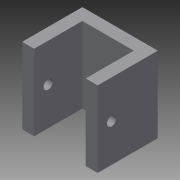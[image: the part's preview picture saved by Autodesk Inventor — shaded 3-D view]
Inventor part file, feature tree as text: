
AUTODESK INVENTOR PART (.ipt)
format: ipt  version: 2013 (Build 170138000, 138)  size: 106,496 bytes
history: native  units: in
note: dims shown in document units (in); Inventor stores cm internally (conversion verified against a paired STEP export)
features: extrude x4, sketch x4
ambient origin geometry x8: Origin, YZ Plane, XZ Plane, XY Plane, X Axis, Y Axis, Z Axis, Center Point
bodies: Solid1 (feature_tree)
feature tree (8):
  extrude  "Extrusion1"  Depth=1.5748in
  extrude  "Extrusion2"  Depth=0.25in
  extrude  "Extrusion3"  Depth=0.25in
  extrude  "Extrusion4"  Depth=0.19in
  sketch  "Sketch1"  dims[d0=1.68in d1=1.5748in]
  sketch  "Sketch2"  dims[d2=0.25in d3=0.0in d4=0.25in]
  sketch  "Sketch3"  dims[d5=1.0in d6=0.0in d7=0.25in]
  sketch  "Sketch4"  dims[d8=1.0in d9=0.0in d10=0.19in d11=3.0in d12=0.0in]
